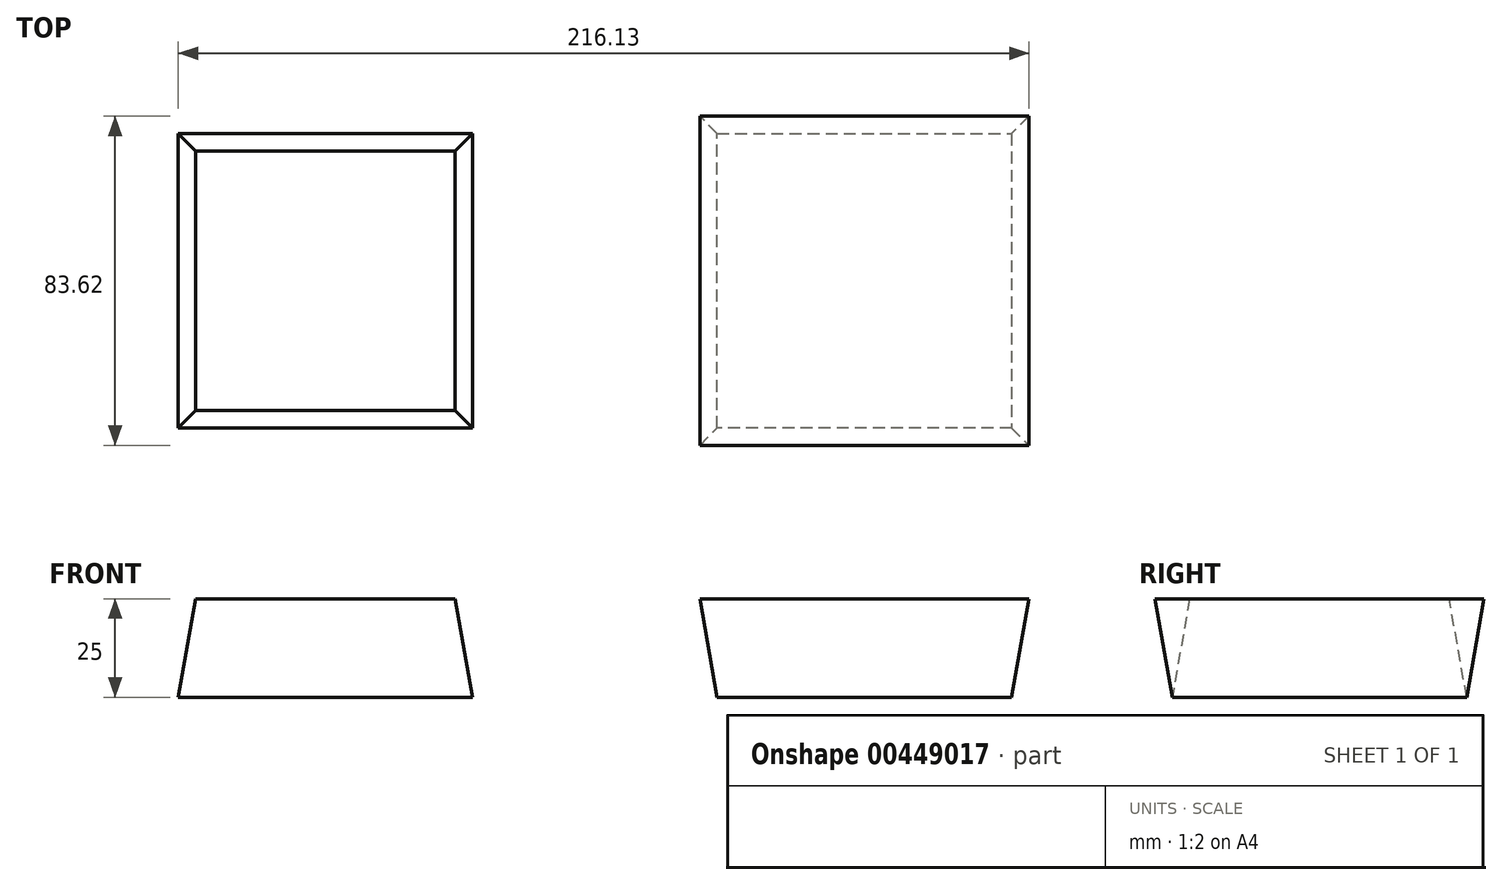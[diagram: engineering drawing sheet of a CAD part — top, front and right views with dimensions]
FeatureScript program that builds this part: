
annotation { "Feature Type Name" : "Feature", "Feature Type Description" : "" }
export const myFeature = defineFeature(function(context is Context, id is Id, definition is map)
    precondition{}
    {
        {
            var Q0;
            Q0=qCreatedBy(makeId("Top.planeOp"),FACE);
            var sketch = newSketch(context, id + "F0", { "sketchPlane" : qUnion([Q0])});
            skLineSegment(sketch, "E0.bottom", {"start": v(-37.4, 37.4) * mm, "end": v(37.4, 37.4) * mm});
            skLineSegment(sketch, "E0.top", {"start": v(-37.4, -37.4) * mm, "end": v(37.4, -37.4) * mm});
            skLineSegment(sketch, "E0.left", {"start": v(-37.4, 37.4) * mm, "end": v(-37.4, -37.4) * mm});
            skLineSegment(sketch, "E0.right", {"start": v(37.4, 37.4) * mm, "end": v(37.4, -37.4) * mm});
            skPoint(sketch, "E0.middle", {"position": v(0, 0) * mm});
            skLineSegment(sketch, "E1.bottom", {"start": v(99.51, 37.4) * mm, "end": v(174.32, 37.4) * mm});
            skLineSegment(sketch, "E1.top", {"start": v(99.51, -37.4) * mm, "end": v(174.32, -37.4) * mm});
            skLineSegment(sketch, "E1.left", {"start": v(99.51, 37.4) * mm, "end": v(99.51, -37.4) * mm});
            skLineSegment(sketch, "E1.right", {"start": v(174.32, 37.4) * mm, "end": v(174.32, -37.4) * mm});
            skPoint(sketch, "E1.middle", {"position": v(136.92, 0) * mm});
            skSolve(sketch);
        }
        {
            var Q0;
            Q0=makeQuery(id+"F0.imprint","IMPRINT",FACE,{"disambiguationData":[TD([[makeQuery(id+"F0.imprint","IMPRINT",EDGE,{"derivedFrom":sQuery(id+"F0.wireOp",EDGE,"E0.bottom")}),-1.0]])]});
            extrude(context, id + "F1", {"entities" : qUnion([Q0]), "depth" : 25 * mm, "hasDraft" : true, "draftAngle" : 10 * degree, "draftPullDirection" : true});
        }
        {
            var Q0;
            Q0=makeQuery(id+"F0.imprint","IMPRINT",FACE,{"disambiguationData":[TD([[makeQuery(id+"F0.imprint","IMPRINT",EDGE,{"derivedFrom":sQuery(id+"F0.wireOp",EDGE,"E1.bottom")}),-1.0]])]});
            extrude(context, id + "F2", {"entities" : qUnion([Q0]), "depth" : 25 * mm, "hasDraft" : true, "draftAngle" : 10 * degree});
        }
    });
